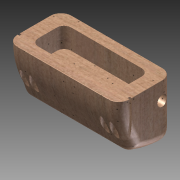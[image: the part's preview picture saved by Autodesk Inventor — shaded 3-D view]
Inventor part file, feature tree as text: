
AUTODESK INVENTOR PART (.ipt)
format: ipt  version: 2015 (Build 190159000, 159)  size: 316,416 bytes
history: native  units: in
note: dims shown in document units (in); Inventor stores cm internally (conversion verified against a paired STEP export)
features: extrude x5, fillet x5, sketch x4, hole x2, plane x1, mirror x1
ambient origin geometry x8: Origin, YZ Plane, XZ Plane, XY Plane, X Axis, Y Axis, Z Axis, Center Point
bodies: Solid1 (feature_tree)
feature tree (18):
  sketch  "Sketch1"  dims[d0=3.17in d1=1.53in d2=1.6in d3=0.0in]
  extrude  "Extrusion1"  Depth=1.53in
  fillet  "Fillet3"  Radius=1.6in
  sketch  "Sketch5"  dims[d20=1.1in d22=1.4in d25=1.15in d26=1.25in]
  extrude  "Extrusion5"  Depth=1.4in
  fillet  "Fillet4"  Radius=1.15in
  fillet  "Fillet5"  Radius=1.25in
  extrude  "Extrusion6"  Depth=0.09in
  fillet  "Fillet6"  Radius=0.13in
  plane  "Work Plane1"
  hole  "Hole1"  [1 undecoded]
  extrude  "Extrusion8"  Depth=0.01in
  hole  "Hole2"  [1 undecoded]
  mirror  "Mirror1"
  fillet  "Fillet7"  Radius=1.0in
  sketch  "Sketch7"  dims[d30=1.0in d31=0.0in d33=0.3in d34=0.2in d35=0.3in d36=1.0in d37=0.0in d39=2.4in d40=0.93in d42=0.0in d43=0.57in d45=0.2in d46=0.27in d47=2.0in d48=1.35in d49=0.2in d50=0.75in d51=0.375in d52=0.25in d53=0.5635in d54=1.0in d55=0.8108in d56=0.3in d57=0.06in d58=1.0in d59=0.0in d60=0.3in d61=0.5in d62=0.29in d63=0.75in d64=0.375in d65=0.25in d66=0.5635in d67=0.35in d68=0.8108in d69=0.01in]
  sketch  "Sketch6"  dims[d27=0.2in d28=0.09in d29=0.13in]
  extrude  "Extrusion7"  Depth=0.01in TaperAngle=0.0deg
note: 2 required parameter values undecoded (feature->parameter linkage not recoverable at this tier; creation-order binding heuristic only, values carry confidence <= 0.55)
